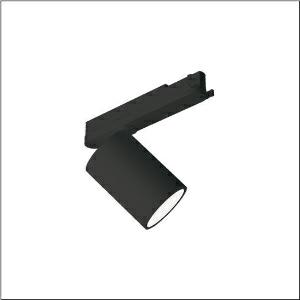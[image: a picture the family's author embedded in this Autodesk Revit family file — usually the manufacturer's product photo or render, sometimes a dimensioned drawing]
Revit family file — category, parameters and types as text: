
# Revit family: spot_31_51sf32mad4b
name_source: partatom
category: Lighting Fixtures
units: mm (PartAtom-declared; Revit-internal decimal feet)

## family parameters
Cut with Voids When Loaded = No
Host = Face
Light Source = No
Part Type = Normal
Room Calculation Point = No
Round Connector Dimension = Use Diameter
Shared = No

## types (1)
- --- (1 x LED, 5140 lm, 41.6 W, 4000K)
    Apparent Load = 42 VA
    CIE Flux Codes = 93 97 99 100 100
    Color Rendering = 90
    Color Temperature = 4000K
    Default Elevation = 1800 mm
    Description = Spot 31, directional spotlight, light control with lens, of PMMA, LED rated luminous flux: 4.930lm, light colour: 940, control gear: ECG Multilumen, with 3-phase adapter, mains connection: 220..240V, AC, 50/60Hz, of aluminium, jet black (RAL 9005), length: 213mm, diameter: 90mm, protection rating (complete): IP20, insulation class (complete): insulation class I (protective earthing), certification: CE, impact resistance: IK02, permissible ambient temperature for indoor applications: -20..+40°C, packaging unit: 1 piece
    Height = 175 mm
    Lamp = 1 x LED
    Lamp Light Flux = 5140 lm
    Lamp Power = 41.6 W
    Lamp count = 1
    Length = 90 mm
    Luminous efficacy = 124 lm/W
    Manufacturer = Siteco
    ModVariant = No
    Model = 51SF32MAD4B
    Mounting Place = Ceiling
    Mounting Type = Pendant
    Number of Poles = 1
    OnlyDefault = Yes
    Power Factor = 1
    Product Name = Spot 31
    Product group = directional spotlight
    ProductGroupID = 905
    Protection Class = Protection class I
    Protection Degree = IP 20
    RLX_Detail_Level = 1
    RLX_Emergency_Light_Flux = 0 lm
    RLX_Emergency_Type = 0
    RLX_Emergency_Type_DB = No
    RlxData = <blob elided: 20909 chars, md5=8ee034ff>
    Socket = socket
    Standby Power = 0 W
    System Light Flux = 5140 lm
    System Power = 42 W
    Type Comments = factory setting: luminous flux: 100 % | (ON | ON | ON | ON) | 1050 mA
    Type Image = l_1273723.jpg
    URL = http://relux.com
    VarID = @adj_096211
    Voltage = 0 V
    Weight = 0.00 kg
    Width = 0 mm  [stored 0 ft]

note: [stored X ft] marks values corroborated as IEEE doubles in the binary element streams (Revit-internal decimal feet)

## geometry (parser evidence)
native form markers: Blend x4, Sweep x11
no freeform markers — native parametric forms only
